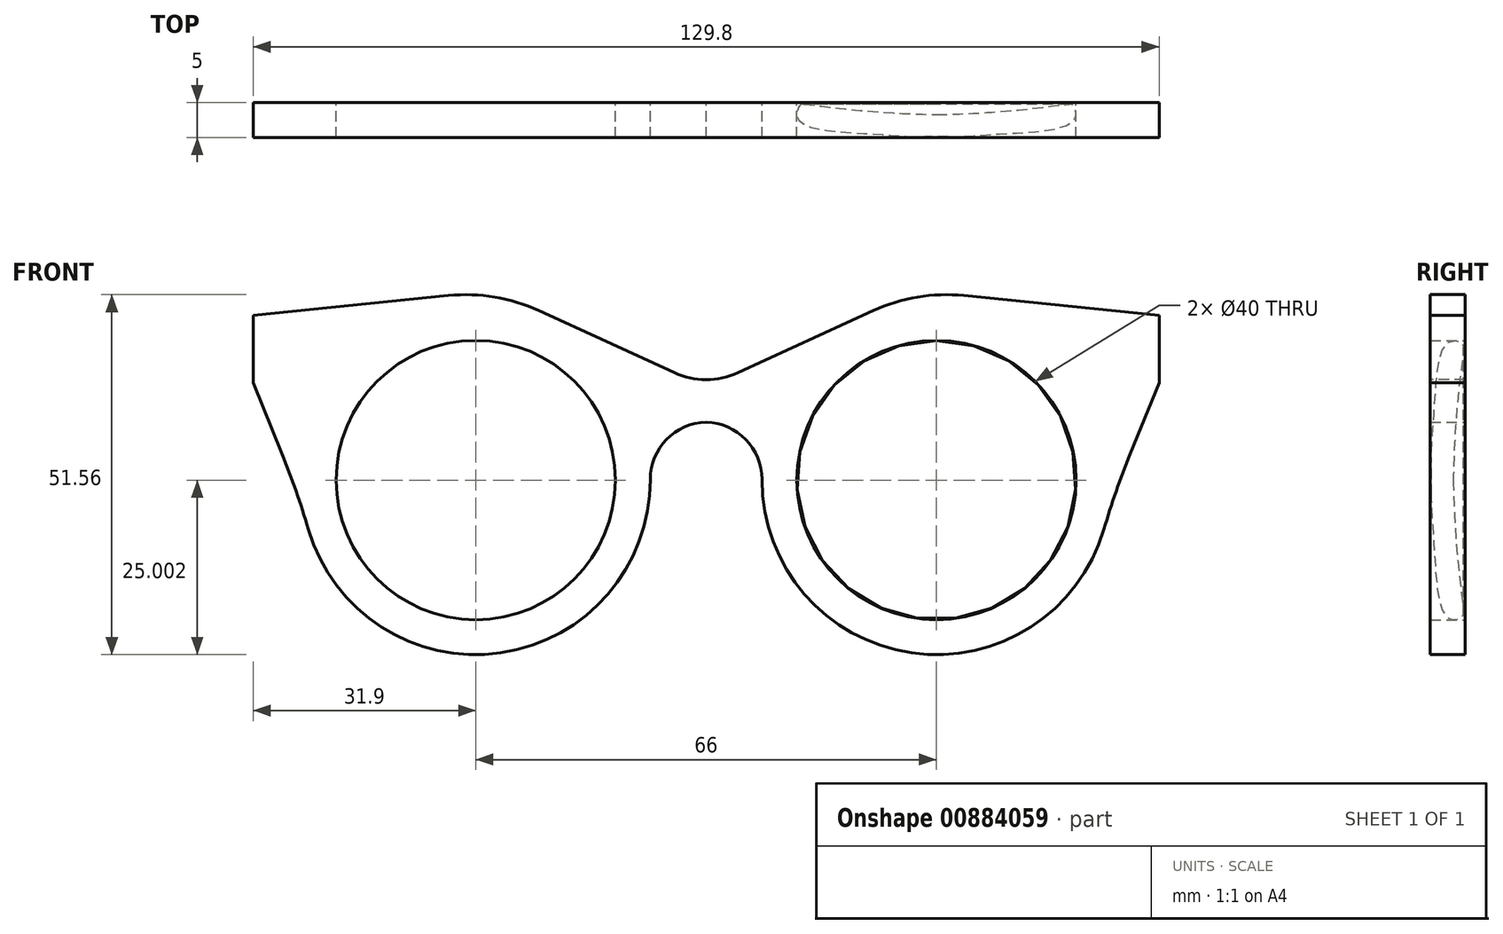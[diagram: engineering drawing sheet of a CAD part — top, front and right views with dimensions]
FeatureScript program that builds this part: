
annotation { "Feature Type Name" : "Feature", "Feature Type Description" : "" }
export const myFeature = defineFeature(function(context is Context, id is Id, definition is map)
    precondition{}
    {
        {
            var Q0;
            Q0=qCreatedBy(makeId("Front.planeOp"),FACE);
            var sketch = newSketch(context, id + "F0", { "sketchPlane" : qUnion([Q0])});
            skCircle(sketch, "E0", {"center": v(33, -5.45) * mm, "radius": 20 * mm});
            skCircle(sketch, "E1", {"center": v(33, -5.45) * mm, "radius": 25 * mm});
            skLineSegment(sketch, "E2", {"start": v(8.06, -3.72) * mm, "end": v(8.06, 2.85) * mm});
            skLineSegment(sketch, "E3", {"start": v(8.06, 2.85) * mm, "end": v(0, 2.85) * mm});
            skLineSegment(sketch, "E4", {"start": v(0, 2.85) * mm, "end": v(0, 7.85) * mm});
            skLineSegment(sketch, "E5", {"start": v(0, 7.85) * mm, "end": v(23.95, 18.83) * mm});
            skLineSegment(sketch, "E6", {"start": v(36.91, 20.98) * mm, "end": v(64.9, 18.12) * mm});
            skLineSegment(sketch, "E7", {"start": v(64.9, 18.12) * mm, "end": v(64.9, 8.5) * mm});
            skLineSegment(sketch, "E8", {"start": v(64.9, 8.5) * mm, "end": v(57.73, -9.14) * mm});
            skPoint(sketch, "E9.visualSharp", {"position": v(8.06, 2.85) * mm});
            skLineSegment(sketch, "E9.filletArc", {"start": v(8.06, 2.85) * mm, "end": v(8.06, 2.85) * mm});
            skPoint(sketch, "E10.visualSharp", {"position": v(30.14, 21.67) * mm});
            skArc(sketch, "E10.filletArc", {"start": v(36.91, 20.98) * mm, "mid": v(30.29, 20.77) * mm, "end": v(23.95, 18.83) * mm});
            skSolve(sketch);
        }
        {
            var Q0;
            {var subQ0=sQuery(id+"F0.wireOp",EDGE,"E2");Q0=makeQuery(id+"F0.imprint","IMPRINT",FACE,{"disambiguationData":[TD([[makeQuery(id+"F0.imprint","IMPRINT",EDGE,{"derivedFrom":subQ0}),-1.0]])]});}
            var Q1;
            Q1=makeQuery(id+"F0.imprint","IMPRINT",FACE,{"disambiguationData":[TD([[makeQuery(id+"F0.imprint","IMPRINT",EDGE,{"derivedFrom":sQuery(id+"F0.wireOp",EDGE,"E0")}),-1.0]])]});
            extrude(context, id + "F1", {"entities" : qUnion([Q0, Q1]), "depth" : 5 * mm, "offsetDistance" : 25 * mm});
        }
        {
            var Q0;
            Q0=makeQuery(id+"F1.opExtrude","SWEPT_EDGE",EDGE,{"disambiguationData":[OSD([sQuery(id+"F0.wireOp",EDGE,"E1"),sQuery(id+"F0.wireOp",EDGE,"E8")])]});
            fillet(context, id + "F2", {"entities" : qUnion([Q0]), "radius" : 112.54 * mm, "tangentPropagation" : true, "allowEdgeOverflow" : false});
        }
        {
            var Q0;
            Q0=makeQuery(id+"F1.opExtrude","SWEPT_BODY",BODY,{"disambiguationData":[OSD([sQuery(id+"F0.wireOp",EDGE,"E0"),sQuery(id+"F0.wireOp",EDGE,"E1"),sQuery(id+"F0.wireOp",EDGE,"E2"),sQuery(id+"F0.wireOp",EDGE,"E3"),sQuery(id+"F0.wireOp",EDGE,"E4"),sQuery(id+"F0.wireOp",EDGE,"E5"),sQuery(id+"F0.wireOp",EDGE,"E6"),sQuery(id+"F0.wireOp",EDGE,"E7"),sQuery(id+"F0.wireOp",EDGE,"E8"),sQuery(id+"F0.wireOp",EDGE,"E10.filletArc")])]});
            var Q1;
            Q1=qCreatedBy(makeId("Right.planeOp"),FACE);
            mirror(context, id + "F3", {"operationType" : NewBodyOperationType.ADD, "entities" : qUnion([Q0]), "mirrorPlane" : qUnion([Q1])});
        }
        {
            var Q0;
            Q0=makeQuery(id+"F1.opExtrude","SWEPT_EDGE",EDGE,{"disambiguationData":[OSD([sQuery(id+"F0.wireOp",EDGE,"E2"),sQuery(id+"F0.wireOp",EDGE,"E3")])]});
            var Q1;
            Q1=makeQuery(id+"F3.opPattern","COPY",EDGE,{"derivedFrom":makeQuery(id+"F1.opExtrude","SWEPT_EDGE",EDGE,{"disambiguationData":[OSD([sQuery(id+"F0.wireOp",EDGE,"E2"),sQuery(id+"F0.wireOp",EDGE,"E3")])]}),"instanceName":"1"});
            fillet(context, id + "F4", {"entities" : qUnion([Q0, Q1]), "radius" : 8.2 * mm, "allowEdgeOverflow" : false});
        }
        {
            var Q0;
            {var subQ0=makeQuery(id+"F1.opExtrude","SWEPT_EDGE",EDGE,{"disambiguationData":[OSD([sQuery(id+"F0.wireOp",EDGE,"E4"),sQuery(id+"F0.wireOp",EDGE,"E5")])]});Q0=makeQuery(id+"FXFWIL5Ah2OxId9_1.boolean.opBoolean","MERGE",EDGE,{"derivedFrom":[subQ0,makeQuery(id+"FXFWIL5Ah2OxId9_1.opPattern","COPY",EDGE,{"derivedFrom":subQ0,"instanceName":"1"})]});}
            fillet(context, id + "F5", {"entities" : qUnion([Q0]), "radius" : 11 * mm, "tangentPropagation" : true, "allowEdgeOverflow" : false});
        }
        {
            var Q0;
            Q0=qCreatedBy(makeId("Right.planeOp"),FACE);
            var Q1;
            Q1=sQuery(id+"F0.wireOp",VERTEX,"E0.center");
            cPlane(context, id + "F6", {"entities" : qUnion([Q0, Q1]), "cplaneType" : CPlaneType.PLANE_POINT, "offset" : 25 * mm, "width" : 150 * mm, "height" : 150 * mm});
        }
        {
            var Q0;
            Q0=qCreatedBy(id+"F6.planeOp",FACE);
            var sketch = newSketch(context, id + "F7", { "sketchPlane" : qUnion([Q0])});
            skLineSegment(sketch, "E11", {"start": v(-1.7, -5.45) * mm, "end": v(-4.88, -5.45) * mm});
            skLineSegment(sketch, "E12", {"start": v(-4.88, -5.45) * mm, "end": v(-4.88, -3.76) * mm});
            skFitSpline(sketch, "E13", {"points": [v(-4.88, -3.76) * mm, v(-4.42, 4.65) * mm, v(-2.56, 14.22) * mm, v(-0.52, 14.22) * mm, v(-0.25, 13.42) * mm, v(-1.05, 6.37) * mm, v(-1.67, -3.76) * mm, v(-1.7, -5.45) * mm], "startDerivative": vector(0.23, 49.03) * mm, "endDerivative": vector(-0.38, -15.48) * mm});
            skSolve(sketch);
        }
        {
            var Q0;
            Q0=makeQuery(id+"F7.imprint","IMPRINT",FACE,{"disambiguationData":[TD([[makeQuery(id+"F7.imprint","IMPRINT",EDGE,{"derivedFrom":sQuery(id+"F7.wireOp",EDGE,"E11")}),-1.0]])]});
            var Q1;
            Q1=sQuery(id+"F7.wireOp",EDGE,"E11");
            revolve(context, id + "F8", {"surfaceOperationType" : NewSurfaceOperationType.NEW, "entities" : qUnion([Q0]), "axis" : qUnion([Q1]), "revolveType" : RevolveType.FULL});
        }
    });
